# Revit family: Sink-Steam-Vessel-Lavatory-KOHLER-Swedna-K-30686IN_1
name_source: partatom
category: Plumbing Fixtures
units: mm (PartAtom-declared; Revit-internal decimal feet)

## family parameters
Cut with Voids When Loaded = No
Host = Face
Maintain Annotation Orientation = No
OmniClass Number = 23.31.13.00
OmniClass Title = Sinks
Part Type = Normal
Room Calculation Point = No
Round Connector Dimension = Use Diameter
Shared = No

## types (1)
- 0-White
    ADA Compliant = No
    Apparent Load = 1610 VA
    Assembly Code = D2010400
    CW Connection = Yes
    Cold Water Inlet = Cold Water Inlet
    Date Modified = 06/24/2022
    Default Elevation = 36"
    Description = Steam Lavatory
    Drain Included = Yes
    Electrical Connector = Yes
    Electrical Note = One Dedicated Circuit Required
    Finish = Kohler-Vitreous_China-0-White
    Generator Material = Premium Metal Construction
    HW Connection = No
    Height = 25 1/8"
    Hot Water Inlet = Hot Water Inlet
    Length = 26 1/8"
    Manufacturer = Kohler Co.
    Master Format 2014 = 22 41 16
    Master Format 2014 Name = Residential Lavatories and Sinks
    Material = Vitreous China
    Model = K-30686IN-0
    Product Name = Swedna
    Secondary Finish = Kohler-Metal-7-Black_Black
    Type = 1
    URL = https://www.kohler.co.in
    Vent Connection = No
    Voltage = 230 V
    Waste Connection = Yes
    Waste Water Outlet = Waste Water Outlet
    WaterSense Certified = No
    Width = 20 3/4"

## geometry (parser evidence)
native form markers: Sweep x5
no freeform markers — native parametric forms only
